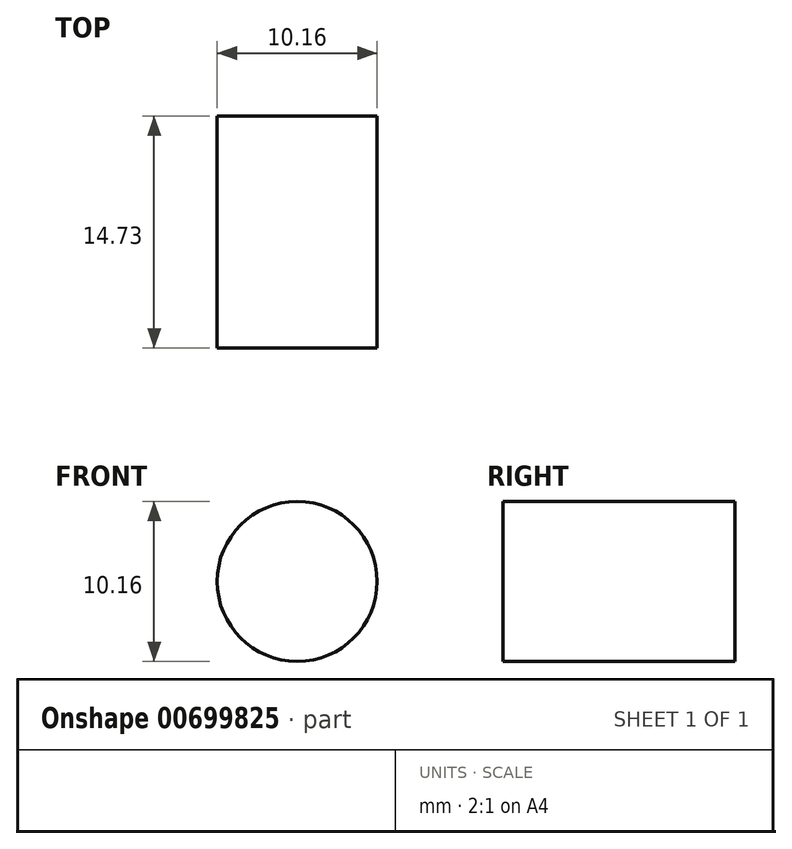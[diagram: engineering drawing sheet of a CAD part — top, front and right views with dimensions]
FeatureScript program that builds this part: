
annotation { "Feature Type Name" : "Feature", "Feature Type Description" : "" }
export const myFeature = defineFeature(function(context is Context, id is Id, definition is map)
    precondition{}
    {
        {
            var Q0;
            Q0=qCreatedBy(makeId("Front.planeOp"),FACE);
            var sketch = newSketch(context, id + "F0", { "sketchPlane" : qUnion([Q0])});
            skCircle(sketch, "E0", {"center": v(0, 0) * mm, "radius": 5.08 * mm});
            skSolve(sketch);
        }
        {
            var Q0;
            Q0=qSketchRegion(id+"F0",true);
            extrude(context, id + "F1", {"entities" : qUnion([Q0]), "depth" : 14.73 * mm});
        }
    });
